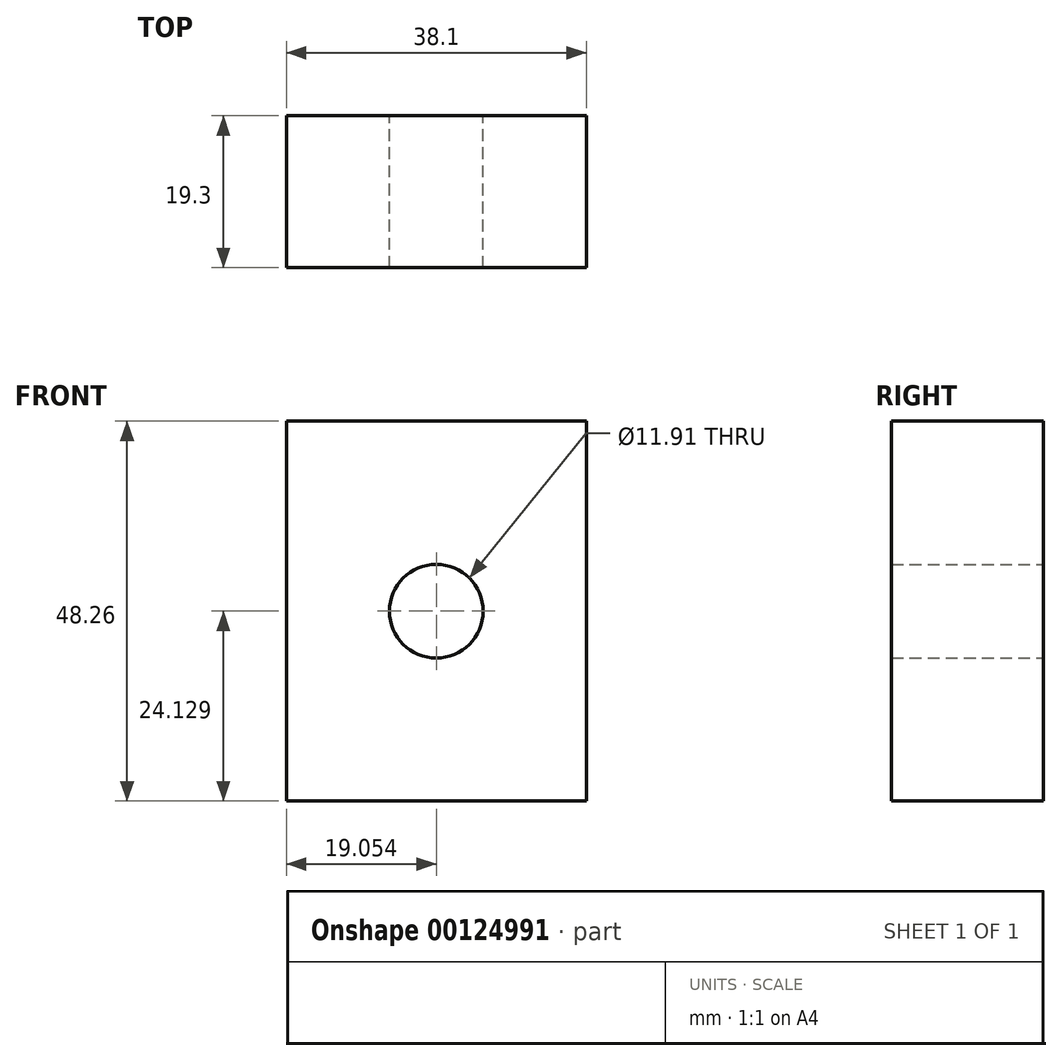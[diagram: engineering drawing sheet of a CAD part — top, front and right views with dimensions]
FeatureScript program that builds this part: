
annotation { "Feature Type Name" : "Feature", "Feature Type Description" : "" }
export const myFeature = defineFeature(function(context is Context, id is Id, definition is map)
    precondition{}
    {
        {
            var Q0;
            Q0=qCreatedBy(makeId("Front.planeOp"),FACE);
            var sketch = newSketch(context, id + "F0", { "sketchPlane" : qUnion([Q0])});
            skLineSegment(sketch, "E0.bottom", {"start": v(-27.56, 25.7) * mm, "end": v(10.54, 25.7) * mm});
            skLineSegment(sketch, "E0.top", {"start": v(-27.56, -22.55) * mm, "end": v(10.54, -22.55) * mm});
            skLineSegment(sketch, "E0.left", {"start": v(-27.56, 25.7) * mm, "end": v(-27.56, -22.55) * mm});
            skLineSegment(sketch, "E0.right", {"start": v(10.54, 25.7) * mm, "end": v(10.54, -22.55) * mm});
            skCircle(sketch, "E1", {"center": v(-8.5, 1.58) * mm, "radius": 5.95 * mm});
            skPoint(sketch, "E1.centerSnap0", {"position": v(10.54, 1.58) * mm});
            skPoint(sketch, "E1.centerSnap1", {"position": v(-8.5, 25.7) * mm});
            skSolve(sketch);
        }
        {
            var Q0;
            Q0=makeQuery(id+"F0.imprint","IMPRINT",FACE,{"disambiguationData":[TD([[makeQuery(id+"F0.imprint","IMPRINT",EDGE,{"derivedFrom":sQuery(id+"F0.wireOp",EDGE,"E0.bottom")}),-1.0]])]});
            extrude(context, id + "F1", {"entities" : qUnion([Q0]), "depth" : 19.3 * mm});
        }
    });
